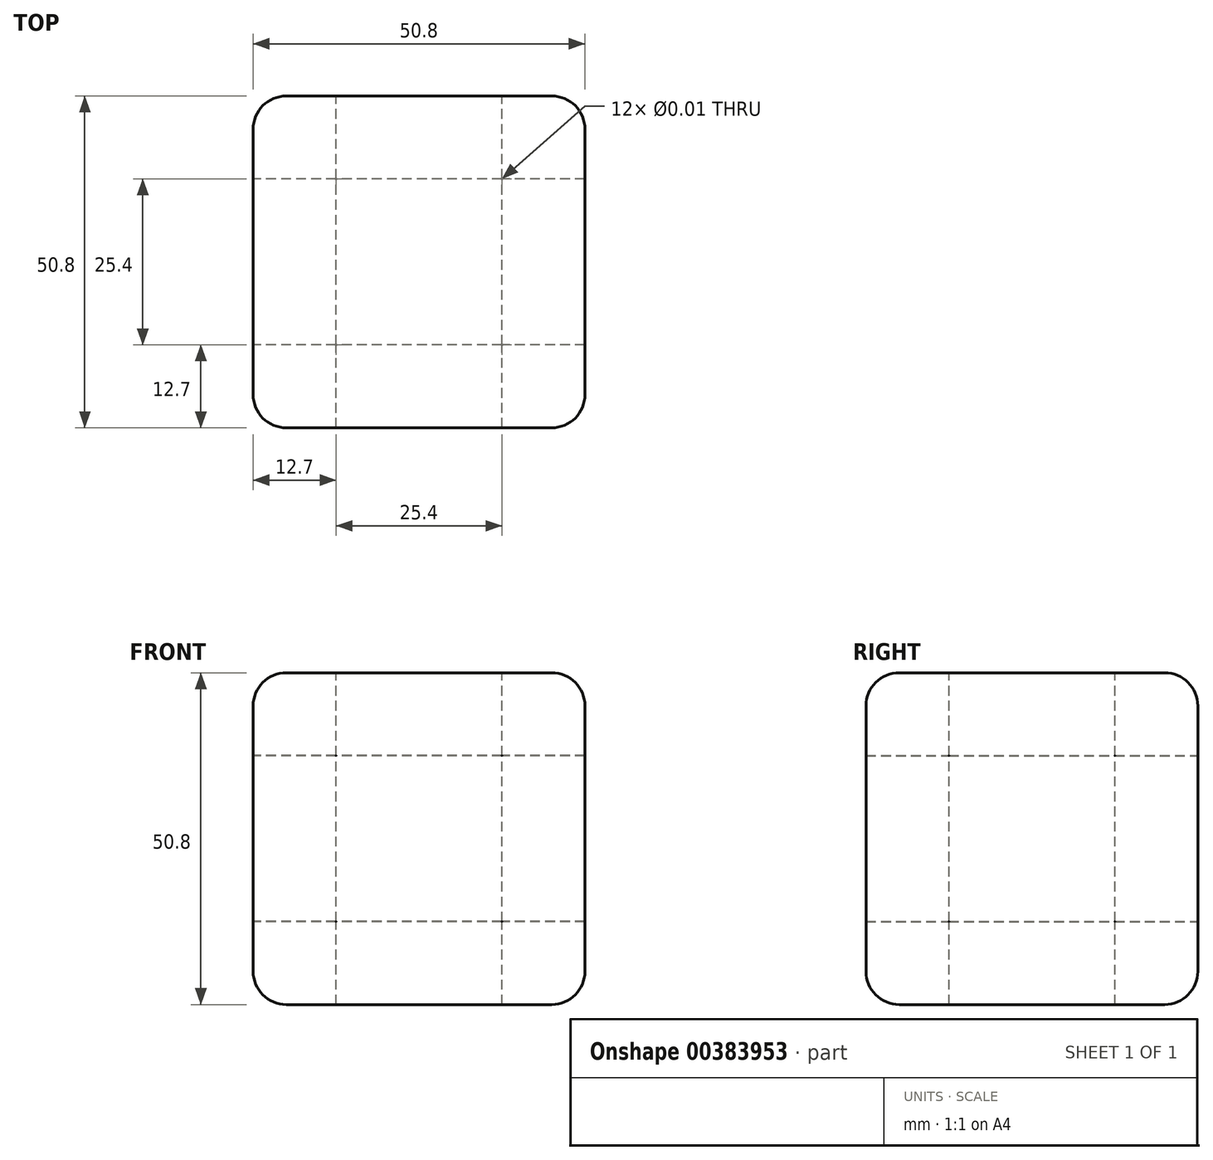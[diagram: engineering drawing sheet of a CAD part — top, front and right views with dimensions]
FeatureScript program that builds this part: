
annotation { "Feature Type Name" : "Feature", "Feature Type Description" : "" }
export const myFeature = defineFeature(function(context is Context, id is Id, definition is map)
    precondition{}
    {
        {
            var Q0;
            Q0=qCreatedBy(makeId("Front.planeOp"),FACE);
            var sketch = newSketch(context, id + "F0", { "sketchPlane" : qUnion([Q0])});
            skLineSegment(sketch, "E0.bottom", {"start": v(0, 0) * mm, "end": v(50.8, 0) * mm});
            skLineSegment(sketch, "E0.top", {"start": v(0, 50.8) * mm, "end": v(50.8, 50.8) * mm});
            skLineSegment(sketch, "E0.left", {"start": v(0, 0) * mm, "end": v(0, 50.8) * mm});
            skLineSegment(sketch, "E0.right", {"start": v(50.8, 0) * mm, "end": v(50.8, 50.8) * mm});
            skPoint(sketch, "E1", {"position": v(12.7, 12.7) * mm});
            skPoint(sketch, "E2", {"position": v(38.1, 12.7) * mm});
            skPoint(sketch, "E3", {"position": v(38.1, 38.1) * mm});
            skPoint(sketch, "E4", {"position": v(12.7, 38.1) * mm});
            skSolve(sketch);
        }
        {
            var Q0;
            Q0=makeQuery(id+"F0.imprint","IMPRINT",FACE,{"disambiguationData":[TD([[makeQuery(id+"F0.imprint","IMPRINT",EDGE,{"derivedFrom":sQuery(id+"F0.wireOp",EDGE,"E0.bottom")}),1.0]])]});
            extrude(context, id + "F1", {"entities" : qUnion([Q0]), "depth" : 50.8 * mm});
        }
        {
            var Q0;
            Q0=makeQuery(id+"F1.opExtrude","SWEPT_FACE",FACE,{"disambiguationData":[OSD([sQuery(id+"F0.wireOp",EDGE,"E0.left")])]});
            var sketch = newSketch(context, id + "F2", { "sketchPlane" : qUnion([Q0])});
            skPoint(sketch, "E5", {"position": v(12.7, 38.1) * mm});
            skPoint(sketch, "E6", {"position": v(38.1, 38.1) * mm});
            skPoint(sketch, "E7", {"position": v(38.1, 12.7) * mm});
            skPoint(sketch, "E8", {"position": v(12.7, 12.7) * mm});
            skSolve(sketch);
        }
        {
            var Q0;
            Q0=sQuery(id+"F2.wireOp",VERTEX,"E5");
            var Q1;
            Q1=sQuery(id+"F2.wireOp",VERTEX,"E6");
            var Q2;
            Q2=sQuery(id+"F2.wireOp",VERTEX,"E7");
            var Q3;
            Q3=sQuery(id+"F2.wireOp",VERTEX,"E8");
            var Q4;
            Q4=makeQuery(id+"F1.opExtrude","SWEPT_BODY",BODY,{"disambiguationData":[OSD([sQuery(id+"F0.wireOp",EDGE,"E0.bottom"),sQuery(id+"F0.wireOp",EDGE,"E0.top"),sQuery(id+"F0.wireOp",EDGE,"E0.left"),sQuery(id+"F0.wireOp",EDGE,"E0.right")])]});
            hole(context, id + "F3", {"style" : HoleStyle.SIMPLE, "endStyle" : HoleEndStyle.THROUGH, "standardTappedOrClearance" : lookupTablePath({ "standard" : "ANSI", "size" : "3/8 (0.38)", "type" : "Drilled" }), "standardBlindInLast" : lookupTablePath({ "standard" : "ANSI", "size" : "3/8", "type" : "Drilled" }), "holeDiameter" : 3 / 203.2 * mm, "isTappedThrough" : true, "tappedDepth" : 12.7 * mm, "tapClearance" : 3, "locations" : qUnion([Q0, Q1, Q2, Q3]), "scope" : qUnion([Q4])});
        }
        {
            var Q0;
            Q0=sQuery(id+"F0.wireOp",VERTEX,"E3");
            var Q1;
            Q1=sQuery(id+"F0.wireOp",VERTEX,"E4");
            var Q2;
            Q2=sQuery(id+"F0.wireOp",VERTEX,"E1");
            var Q3;
            Q3=sQuery(id+"F0.wireOp",VERTEX,"E2");
            var Q4;
            Q4=makeQuery(id+"F1.opExtrude","SWEPT_BODY",BODY,{"disambiguationData":[OSD([sQuery(id+"F0.wireOp",EDGE,"E0.bottom"),sQuery(id+"F0.wireOp",EDGE,"E0.top"),sQuery(id+"F0.wireOp",EDGE,"E0.left"),sQuery(id+"F0.wireOp",EDGE,"E0.right")])]});
            hole(context, id + "F4", {"style" : HoleStyle.SIMPLE, "endStyle" : HoleEndStyle.THROUGH, "oppositeDirection" : true, "standardTappedOrClearance" : lookupTablePath({ "standard" : "ANSI", "size" : "3/8 (0.38)", "type" : "Drilled" }), "standardBlindInLast" : lookupTablePath({ "standard" : "ANSI", "size" : "3/8", "type" : "Drilled" }), "holeDiameter" : 3 / 203.2 * mm, "isTappedThrough" : true, "tappedDepth" : 12.7 * mm, "tapClearance" : 3, "locations" : qUnion([Q0, Q1, Q2, Q3]), "scope" : qUnion([Q4])});
        }
        {
            var Q0;
            Q0=makeQuery(id+"F1.opExtrude","SWEPT_FACE",FACE,{"disambiguationData":[OSD([sQuery(id+"F0.wireOp",EDGE,"E0.top")])]});
            var sketch = newSketch(context, id + "F5", { "sketchPlane" : qUnion([Q0])});
            skPoint(sketch, "E9", {"position": v(12.7, -12.7) * mm});
            skPoint(sketch, "E10", {"position": v(38.1, -12.7) * mm});
            skPoint(sketch, "E11", {"position": v(38.1, -38.1) * mm});
            skPoint(sketch, "E12", {"position": v(12.7, -38.1) * mm});
            skSolve(sketch);
        }
        {
            var Q0;
            Q0=sQuery(id+"F5.wireOp",VERTEX,"E9");
            var Q1;
            Q1=sQuery(id+"F5.wireOp",VERTEX,"E10");
            var Q2;
            Q2=sQuery(id+"F5.wireOp",VERTEX,"E11");
            var Q3;
            Q3=sQuery(id+"F5.wireOp",VERTEX,"E12");
            var Q4;
            Q4=makeQuery(id+"F1.opExtrude","SWEPT_BODY",BODY,{"disambiguationData":[OSD([sQuery(id+"F0.wireOp",EDGE,"E0.bottom"),sQuery(id+"F0.wireOp",EDGE,"E0.top"),sQuery(id+"F0.wireOp",EDGE,"E0.left"),sQuery(id+"F0.wireOp",EDGE,"E0.right")])]});
            hole(context, id + "F6", {"style" : HoleStyle.SIMPLE, "endStyle" : HoleEndStyle.THROUGH, "standardTappedOrClearance" : lookupTablePath({ "standard" : "ANSI", "size" : "3/8 (0.38)", "type" : "Drilled" }), "standardBlindInLast" : lookupTablePath({ "standard" : "ANSI", "size" : "3/8", "type" : "Drilled" }), "holeDiameter" : 3 / 203.2 * mm, "isTappedThrough" : true, "tappedDepth" : 12.7 * mm, "tapClearance" : 3, "locations" : qUnion([Q0, Q1, Q2, Q3]), "scope" : qUnion([Q4])});
        }
        {
            var Q0;
            Q0=makeQuery(id+"F1.opExtrude","CAP_EDGE",EDGE,{"disambiguationData":[OSD([sQuery(id+"F0.wireOp",EDGE,"E0.top")])],"isStart":false});
            var Q1;
            Q1=makeQuery(id+"F1.opExtrude","SWEPT_EDGE",EDGE,{"disambiguationData":[OSD([sQuery(id+"F0.wireOp",EDGE,"E0.top"),sQuery(id+"F0.wireOp",EDGE,"E0.left")])]});
            var Q2;
            Q2=makeQuery(id+"F1.opExtrude","SWEPT_EDGE",EDGE,{"disambiguationData":[OSD([sQuery(id+"F0.wireOp",EDGE,"E0.top"),sQuery(id+"F0.wireOp",EDGE,"E0.right")])]});
            var Q3;
            Q3=makeQuery(id+"F1.opExtrude","CAP_EDGE",EDGE,{"disambiguationData":[OSD([sQuery(id+"F0.wireOp",EDGE,"E0.top")])],"isStart":true});
            var Q4;
            Q4=makeQuery(id+"F1.opExtrude","CAP_EDGE",EDGE,{"disambiguationData":[OSD([sQuery(id+"F0.wireOp",EDGE,"E0.right")])],"isStart":true});
            var Q5;
            Q5=makeQuery(id+"F1.opExtrude","CAP_EDGE",EDGE,{"disambiguationData":[OSD([sQuery(id+"F0.wireOp",EDGE,"E0.left")])],"isStart":true});
            var Q6;
            Q6=makeQuery(id+"F1.opExtrude","CAP_EDGE",EDGE,{"disambiguationData":[OSD([sQuery(id+"F0.wireOp",EDGE,"E0.bottom")])],"isStart":true});
            var Q7;
            Q7=makeQuery(id+"F1.opExtrude","SWEPT_EDGE",EDGE,{"disambiguationData":[OSD([sQuery(id+"F0.wireOp",EDGE,"E0.bottom"),sQuery(id+"F0.wireOp",EDGE,"E0.right")])]});
            var Q8;
            Q8=makeQuery(id+"F1.opExtrude","SWEPT_EDGE",EDGE,{"disambiguationData":[OSD([sQuery(id+"F0.wireOp",EDGE,"E0.bottom"),sQuery(id+"F0.wireOp",EDGE,"E0.left")])]});
            var Q9;
            Q9=makeQuery(id+"F1.opExtrude","CAP_EDGE",EDGE,{"disambiguationData":[OSD([sQuery(id+"F0.wireOp",EDGE,"E0.bottom")])],"isStart":false});
            var Q10;
            Q10=makeQuery(id+"F1.opExtrude","CAP_EDGE",EDGE,{"disambiguationData":[OSD([sQuery(id+"F0.wireOp",EDGE,"E0.left")])],"isStart":false});
            var Q11;
            Q11=makeQuery(id+"F1.opExtrude","CAP_EDGE",EDGE,{"disambiguationData":[OSD([sQuery(id+"F0.wireOp",EDGE,"E0.right")])],"isStart":false});
            fillet(context, id + "F7", {"entities" : qUnion([Q0, Q1, Q2, Q3, Q4, Q5, Q6, Q7, Q8, Q9, Q10, Q11]), "radius" : 5.08 * mm, "tangentPropagation" : true, "allowEdgeOverflow" : false});
        }
    });
